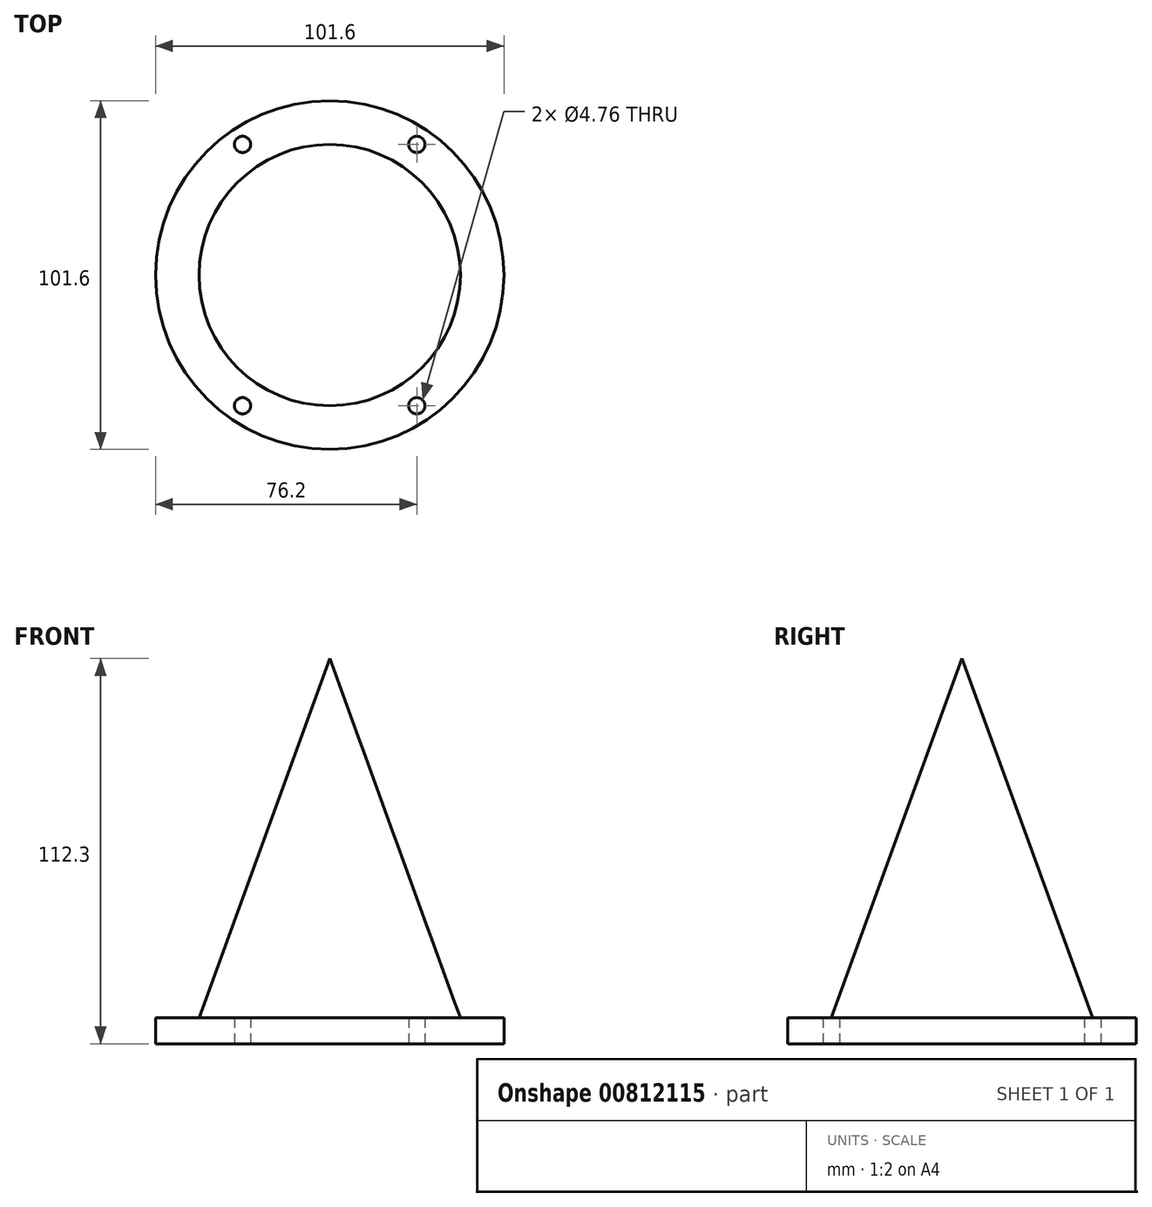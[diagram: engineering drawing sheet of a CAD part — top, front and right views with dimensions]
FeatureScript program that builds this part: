
annotation { "Feature Type Name" : "Feature", "Feature Type Description" : "" }
export const myFeature = defineFeature(function(context is Context, id is Id, definition is map)
    precondition{}
    {
        {
            var Q0;
            Q0=qCreatedBy(makeId("Top.planeOp"),FACE);
            var sketch = newSketch(context, id + "F0", { "sketchPlane" : qUnion([Q0])});
            skCircle(sketch, "E0", {"center": v(0, 0) * mm, "radius": 50.8 * mm});
            skSolve(sketch);
        }
        {
            var Q0;
            Q0=makeQuery(id+"F0.imprint","IMPRINT",FACE,{"disambiguationData":[TD([[makeQuery(id+"F0.imprint","IMPRINT",EDGE,{"derivedFrom":sQuery(id+"F0.wireOp",EDGE,"E0")}),1.0]])]});
            extrude(context, id + "F1", {"entities" : qUnion([Q0]), "depth" : 7.62 * mm, "offsetDistance" : 25.4 * mm});
        }
        {
            var Q0;
            Q0=makeQuery(id+"F1.opExtrude","CAP_FACE",FACE,{"disambiguationData":[OSD([sQuery(id+"F0.wireOp",EDGE,"E0")])],"isStart":false});
            var sketch = newSketch(context, id + "F2", { "sketchPlane" : qUnion([Q0])});
            skCircle(sketch, "E1", {"center": v(0, 0) * mm, "radius": 38.1 * mm});
            skSolve(sketch);
        }
        {
            var Q0;
            Q0=makeQuery(id+"F2.imprint","IMPRINT",FACE,{"disambiguationData":[TD([[makeQuery(id+"F2.imprint","IMPRINT",EDGE,{"derivedFrom":sQuery(id+"F2.wireOp",EDGE,"E1")}),1.0]])]});
            extrude(context, id + "F3", {"entities" : qUnion([Q0]), "operationType" : NewBodyOperationType.ADD, "depth" : 124.2 * mm, "offsetDistance" : 25.4 * mm, "hasDraft" : true, "draftAngle" : 20 * degree, "draftPullDirection" : true});
        }
        {
            var Q0;
            Q0=qCreatedBy(makeId("Top.planeOp"),FACE);
            var sketch = newSketch(context, id + "F4", { "sketchPlane" : qUnion([Q0])});
            skCircle(sketch, "E2.1.0", {"center": v(-25.4, -38.1) * mm, "radius": 2.37 * mm});
            skPoint(sketch, "E2.center", {"position": v(0, 0) * mm});
            skCircle(sketch, "E3", {"center": v(25.4, -38.1) * mm, "radius": 2.38 * mm});
            skLineSegment(sketch, "E4", {"start": v(0, 0) * mm, "end": v(0, -38.1) * mm, "construction": true});
            skLineSegment(sketch, "E5", {"start": v(0, -38.1) * mm, "end": v(25.4, -38.1) * mm, "construction": true});
            skLineSegment(sketch, "E6", {"start": v(25.4, -38.1) * mm, "end": v(-25.4, -38.1) * mm, "construction": true});
            skCircle(sketch, "E7.0.1.0", {"center": v(25.4, 38.1) * mm, "radius": 2.38 * mm});
            skCircle(sketch, "E7.0.1.1", {"center": v(-25.4, 38.1) * mm, "radius": 2.37 * mm});
            skLineSegment(sketch, "E7.direction1", {"start": v(25.4, -38.1) * mm, "end": v(50.8, -38.1) * mm, "construction": true});
            skLineSegment(sketch, "E7.direction2", {"start": v(25.4, -38.1) * mm, "end": v(25.4, 38.1) * mm, "construction": true});
            skSolve(sketch);
        }
        {
            var Q0;
            Q0=makeQuery(id+"F4.imprint","IMPRINT",FACE,{"disambiguationData":[TD([[makeQuery(id+"F4.imprint","IMPRINT",EDGE,{"derivedFrom":sQuery(id+"F4.wireOp",EDGE,"E2.1.0")}),1.0]])]});
            var Q1;
            Q1=makeQuery(id+"F4.imprint","IMPRINT",FACE,{"disambiguationData":[TD([[makeQuery(id+"F4.imprint","IMPRINT",EDGE,{"derivedFrom":sQuery(id+"F4.wireOp",EDGE,"E3")}),1.0]])]});
            var Q2;
            Q2=makeQuery(id+"F4.imprint","IMPRINT",FACE,{"disambiguationData":[TD([[makeQuery(id+"F4.imprint","IMPRINT",EDGE,{"derivedFrom":sQuery(id+"F4.wireOp",EDGE,"E7.0.1.1")}),1.0]])]});
            var Q3;
            Q3=makeQuery(id+"F4.imprint","IMPRINT",FACE,{"disambiguationData":[TD([[makeQuery(id+"F4.imprint","IMPRINT",EDGE,{"derivedFrom":sQuery(id+"F4.wireOp",EDGE,"E7.0.1.0")}),1.0]])]});
            extrude(context, id + "F5", {"entities" : qUnion([Q0, Q1, Q2, Q3]), "operationType" : NewBodyOperationType.REMOVE, "depth" : 25.4 * mm, "offsetDistance" : 25.4 * mm});
        }
    });
